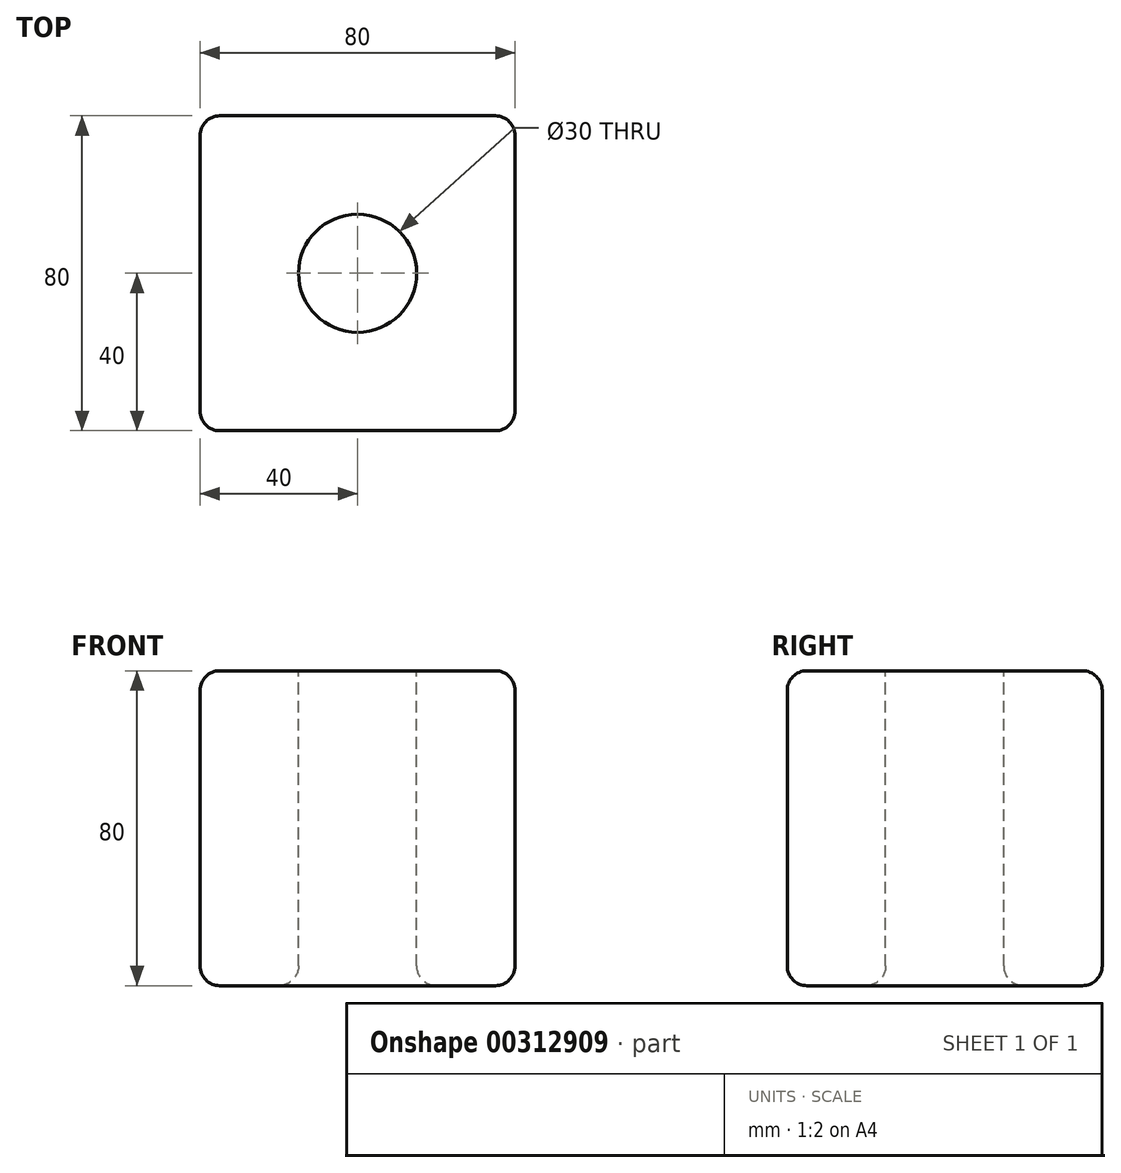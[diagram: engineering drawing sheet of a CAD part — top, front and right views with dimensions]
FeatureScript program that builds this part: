
annotation { "Feature Type Name" : "Feature", "Feature Type Description" : "" }
export const myFeature = defineFeature(function(context is Context, id is Id, definition is map)
    precondition{}
    {
        {
            var Q0;
            Q0=qCreatedBy(makeId("Top.planeOp"),FACE);
            var sketch = newSketch(context, id + "F0", { "sketchPlane" : qUnion([Q0])});
            skLineSegment(sketch, "E0.bottom", {"start": v(40, 40) * mm, "end": v(-40, 40) * mm});
            skLineSegment(sketch, "E0.top", {"start": v(40, -40) * mm, "end": v(-40, -40) * mm});
            skLineSegment(sketch, "E0.left", {"start": v(40, 40) * mm, "end": v(40, -40) * mm});
            skLineSegment(sketch, "E0.right", {"start": v(-40, 40) * mm, "end": v(-40, -40) * mm});
            skPoint(sketch, "E0.middle", {"position": v(0, 0) * mm});
            skSolve(sketch);
        }
        {
            var Q0;
            Q0=makeQuery(id+"F0.imprint","IMPRINT",FACE,{"disambiguationData":[TD([[makeQuery(id+"F0.imprint","IMPRINT",EDGE,{"derivedFrom":sQuery(id+"F0.wireOp",EDGE,"E0.bottom")}),1.0]])]});
            extrude(context, id + "F1", {"entities" : qUnion([Q0]), "endBound" : BoundingType.SYMMETRIC, "depth" : 80 * mm});
        }
        {
            var Q0;
            Q0=makeQuery(id+"F1.opExtrude","CAP_EDGE",EDGE,{"disambiguationData":[OSD([sQuery(id+"F0.wireOp",EDGE,"E0.left")])],"isStart":false});
            var Q1;
            Q1=makeQuery(id+"F1.opExtrude","SWEPT_EDGE",EDGE,{"disambiguationData":[OSD([sQuery(id+"F0.wireOp",EDGE,"E0.top"),sQuery(id+"F0.wireOp",EDGE,"E0.left")])]});
            var Q2;
            Q2=makeQuery(id+"F1.opExtrude","CAP_EDGE",EDGE,{"disambiguationData":[OSD([sQuery(id+"F0.wireOp",EDGE,"E0.left")])],"isStart":true});
            var Q3;
            Q3=makeQuery(id+"F1.opExtrude","SWEPT_EDGE",EDGE,{"disambiguationData":[OSD([sQuery(id+"F0.wireOp",EDGE,"E0.bottom"),sQuery(id+"F0.wireOp",EDGE,"E0.left")])]});
            var Q4;
            Q4=makeQuery(id+"F1.opExtrude","CAP_EDGE",EDGE,{"disambiguationData":[OSD([sQuery(id+"F0.wireOp",EDGE,"E0.bottom")])],"isStart":false});
            var Q5;
            Q5=makeQuery(id+"F1.opExtrude","SWEPT_EDGE",EDGE,{"disambiguationData":[OSD([sQuery(id+"F0.wireOp",EDGE,"E0.bottom"),sQuery(id+"F0.wireOp",EDGE,"E0.right")])]});
            var Q6;
            Q6=makeQuery(id+"F1.opExtrude","CAP_EDGE",EDGE,{"disambiguationData":[OSD([sQuery(id+"F0.wireOp",EDGE,"E0.bottom")])],"isStart":true});
            var Q7;
            Q7=makeQuery(id+"F1.opExtrude","SWEPT_FACE",FACE,{"disambiguationData":[OSD([sQuery(id+"F0.wireOp",EDGE,"E0.top")])]});
            var Q8;
            Q8=makeQuery(id+"F1.opExtrude","SWEPT_FACE",FACE,{"disambiguationData":[OSD([sQuery(id+"F0.wireOp",EDGE,"E0.right")])]});
            fillet(context, id + "F2", {"entities" : qUnion([Q0, Q1, Q2, Q3, Q4, Q5, Q6, Q7, Q8]), "radius" : 5 * mm, "tangentPropagation" : true, "allowEdgeOverflow" : false});
        }
        {
            var Q0;
            Q0=makeQuery(id+"F1.opExtrude","CAP_FACE",FACE,{"disambiguationData":[OSD([sQuery(id+"F0.wireOp",EDGE,"E0.bottom"),sQuery(id+"F0.wireOp",EDGE,"E0.top"),sQuery(id+"F0.wireOp",EDGE,"E0.left"),sQuery(id+"F0.wireOp",EDGE,"E0.right")])],"isStart":false});
            var sketch = newSketch(context, id + "F3", { "sketchPlane" : qUnion([Q0])});
            skCircle(sketch, "E1", {"center": v(0, 0) * mm, "radius": 15 * mm});
            skSolve(sketch);
        }
        {
            var Q0;
            Q0=makeQuery(id+"F3.imprint","IMPRINT",FACE,{"disambiguationData":[TD([[makeQuery(id+"F3.imprint","IMPRINT",EDGE,{"derivedFrom":sQuery(id+"F3.wireOp",EDGE,"E1")}),1.0]])]});
            extrude(context, id + "F4", {"entities" : qUnion([Q0]), "operationType" : NewBodyOperationType.REMOVE, "endBound" : BoundingType.THROUGH_ALL, "oppositeDirection" : true, "depth" : 25 * mm});
        }
        {
            var Q0;
            Q0=makeQuery(id+"F4.boolean.opBoolean","COPY",EDGE,{"derivedFrom":makeQuery(id+"F4.opExtrude","CAP_EDGE",EDGE,{"disambiguationData":[OSD([sQuery(id+"F3.wireOp",EDGE,"E1")])],"isStart":true})});
            var Q1;
            Q1=makeQuery(id+"F4.boolean.opBoolean","INTERSECT",EDGE,{"derivedFrom":[makeQuery(id+"F1.opExtrude","CAP_FACE",FACE,{"disambiguationData":[OSD([sQuery(id+"F0.wireOp",EDGE,"E0.bottom"),sQuery(id+"F0.wireOp",EDGE,"E0.top"),sQuery(id+"F0.wireOp",EDGE,"E0.left"),sQuery(id+"F0.wireOp",EDGE,"E0.right")])],"isStart":true}),makeQuery(id+"F4.opExtrude","SWEPT_FACE",FACE,{"disambiguationData":[OSD([sQuery(id+"F3.wireOp",EDGE,"E1")])]})]});
            fillet(context, id + "F5", {"entities" : qUnion([Q0, Q1]), "radius" : 5 * mm, "tangentPropagation" : true, "allowEdgeOverflow" : false});
        }
    });
